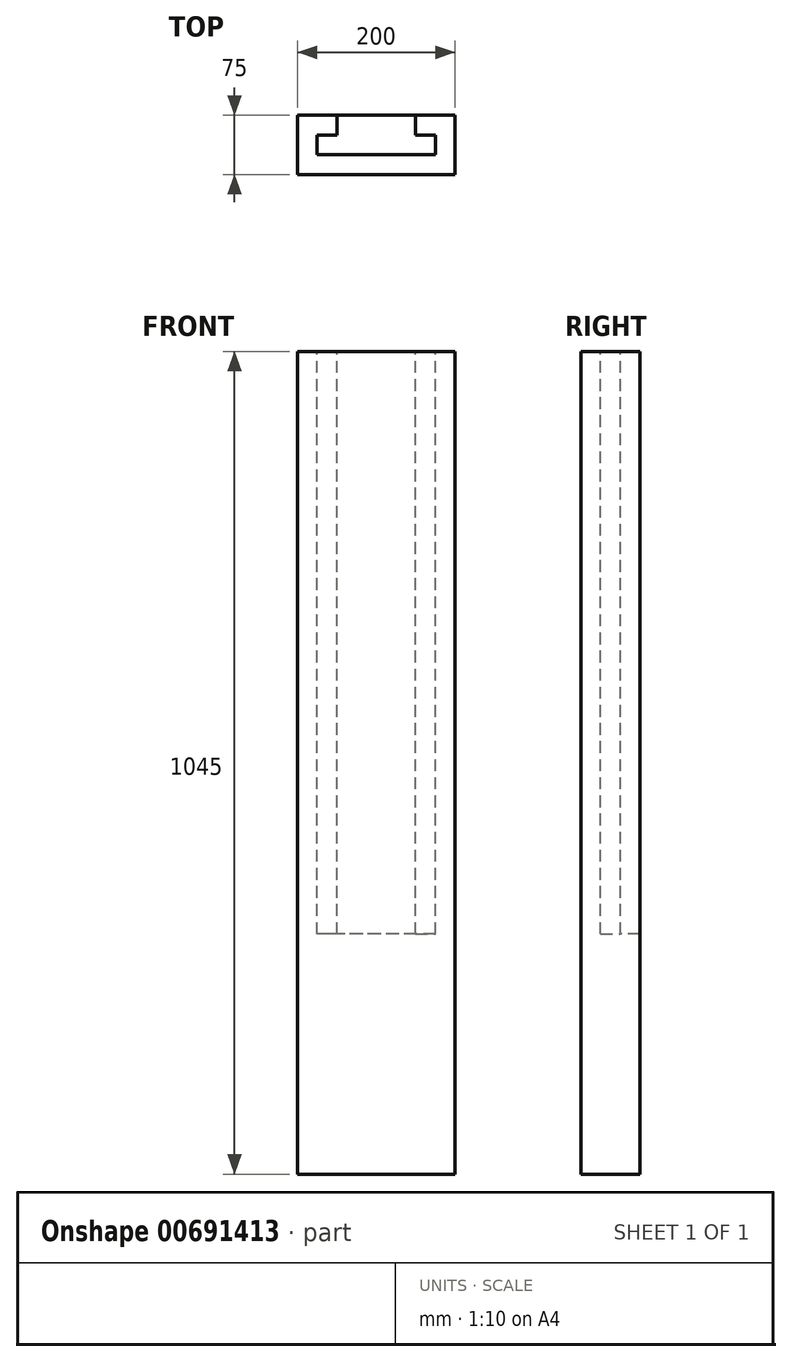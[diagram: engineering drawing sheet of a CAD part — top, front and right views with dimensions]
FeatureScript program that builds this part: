
annotation { "Feature Type Name" : "Feature", "Feature Type Description" : "" }
export const myFeature = defineFeature(function(context is Context, id is Id, definition is map)
    precondition{}
    {
        {
            var Q0;
            Q0=qCreatedBy(makeId("Right.planeOp"),FACE);
            var sketch = newSketch(context, id + "F0", { "sketchPlane" : qUnion([Q0])});
            skLineSegment(sketch, "E0.bottom", {"start": v(37.5, 305) * mm, "end": v(-37.5, 305) * mm});
            skLineSegment(sketch, "E0.top", {"start": v(37.5, -305) * mm, "end": v(-37.5, -305) * mm});
            skLineSegment(sketch, "E0.left", {"start": v(37.5, 305) * mm, "end": v(37.5, -305) * mm});
            skLineSegment(sketch, "E0.right", {"start": v(-37.5, 305) * mm, "end": v(-37.5, -305) * mm});
            skPoint(sketch, "E0.middle", {"position": v(0, 0) * mm});
            skSolve(sketch);
        }
        {
            var Q0;
            Q0=makeQuery(id+"F0.imprint","IMPRINT",FACE,{"disambiguationData":[TD([[makeQuery(id+"F0.imprint","IMPRINT",EDGE,{"derivedFrom":sQuery(id+"F0.wireOp",EDGE,"E0.bottom")}),1.0]])]});
            extrude(context, id + "F1", {"entities" : qUnion([Q0]), "depth" : 200 * mm, "offsetDistance" : 25 * mm});
        }
        {
            var Q0;
            Q0=makeQuery(id+"F1.opExtrude","SWEPT_FACE",FACE,{"disambiguationData":[OSD([sQuery(id+"F0.wireOp",EDGE,"E0.bottom")])]});
            var sketch = newSketch(context, id + "F2", { "sketchPlane" : qUnion([Q0])});
            skLineSegment(sketch, "E1.bottom", {"start": v(50, 37.5) * mm, "end": v(150, 37.5) * mm});
            skLineSegment(sketch, "E1.top", {"start": v(50, -12.5) * mm, "end": v(150, -12.5) * mm});
            skLineSegment(sketch, "E1.left", {"start": v(50, 37.5) * mm, "end": v(50, -12.5) * mm});
            skLineSegment(sketch, "E1.right", {"start": v(150, 37.5) * mm, "end": v(150, -12.5) * mm});
            skLineSegment(sketch, "E2.bottom", {"start": v(50, -12.5) * mm, "end": v(25, -12.5) * mm});
            skLineSegment(sketch, "E2.top", {"start": v(50, 12.5) * mm, "end": v(25, 12.5) * mm});
            skLineSegment(sketch, "E2.left", {"start": v(50, -12.5) * mm, "end": v(50, 12.5) * mm});
            skLineSegment(sketch, "E2.right", {"start": v(25, -12.5) * mm, "end": v(25, 12.5) * mm});
            skLineSegment(sketch, "E3.bottom", {"start": v(150, -12.5) * mm, "end": v(175, -12.5) * mm});
            skLineSegment(sketch, "E3.top", {"start": v(150, 12.5) * mm, "end": v(175, 12.5) * mm});
            skLineSegment(sketch, "E3.left", {"start": v(150, -12.5) * mm, "end": v(150, 12.5) * mm});
            skLineSegment(sketch, "E3.right", {"start": v(175, -12.5) * mm, "end": v(175, 12.5) * mm});
            skSolve(sketch);
        }
        {
            var Q0;
            Q0 = qSketchRegion(id + "F2", true);
            extrude(context, id + "F3", {"entities" : qUnion([Q0]), "operationType" : NewBodyOperationType.REMOVE, "oppositeDirection" : true, "depth" : 525 * mm, "offsetDistance" : 25 * mm});
        }
        {
            var Q0;
            Q0=makeQuery(id+"F1.opExtrude","SWEPT_FACE",FACE,{"disambiguationData":[OSD([sQuery(id+"F0.wireOp",EDGE,"E0.top")])]});
            var sketch = newSketch(context, id + "F4", { "sketchPlane" : qUnion([Q0])});
            skLineSegment(sketch, "E4.bottom", {"start": v(0, 37.5) * mm, "end": v(200, 37.5) * mm});
            skLineSegment(sketch, "E4.top", {"start": v(0, -37.5) * mm, "end": v(200, -37.5) * mm});
            skLineSegment(sketch, "E4.left", {"start": v(0, 37.5) * mm, "end": v(0, -37.5) * mm});
            skLineSegment(sketch, "E4.right", {"start": v(200, 37.5) * mm, "end": v(200, -37.5) * mm});
            skSolve(sketch);
        }
        {
            var Q0;
            Q0=makeQuery(id+"F4.imprint","IMPRINT",FACE,{"disambiguationData":[TD([[makeQuery(id+"F4.imprint","IMPRINT",EDGE,{"derivedFrom":sQuery(id+"F4.wireOp",EDGE,"E4.bottom")}),1.0]])]});
            extrude(context, id + "F5", {"entities" : qUnion([Q0]), "operationType" : NewBodyOperationType.ADD, "depth" : 220 * mm, "offsetDistance" : 25 * mm});
        }
        {
            var Q0;
            Q0=makeQuery(id+"F1.opExtrude","SWEPT_FACE",FACE,{"disambiguationData":[OSD([sQuery(id+"F0.wireOp",EDGE,"E0.bottom")])]});
            var sketch = newSketch(context, id + "F6", { "sketchPlane" : qUnion([Q0])});
            skLineSegment(sketch, "E5", {"start": v(25, 12.5) * mm, "end": v(50, 12.5) * mm});
            skLineSegment(sketch, "E6", {"start": v(50, 12.5) * mm, "end": v(50, 37.5) * mm});
            skLineSegment(sketch, "E7", {"start": v(50, 37.5) * mm, "end": v(0, 37.5) * mm});
            skLineSegment(sketch, "E8", {"start": v(0, 37.5) * mm, "end": v(0, -37.5) * mm});
            skLineSegment(sketch, "E9", {"start": v(0, -37.5) * mm, "end": v(200, -37.5) * mm});
            skLineSegment(sketch, "E10", {"start": v(200, -37.5) * mm, "end": v(200, 37.5) * mm});
            skLineSegment(sketch, "E11", {"start": v(200, 37.5) * mm, "end": v(150, 37.5) * mm});
            skLineSegment(sketch, "E12", {"start": v(150, 37.5) * mm, "end": v(150, 12.5) * mm});
            skLineSegment(sketch, "E13", {"start": v(150, 12.5) * mm, "end": v(175, 12.5) * mm});
            skLineSegment(sketch, "E14", {"start": v(175, 12.5) * mm, "end": v(175, -12.5) * mm});
            skLineSegment(sketch, "E15", {"start": v(175, -12.5) * mm, "end": v(25, -12.5) * mm});
            skLineSegment(sketch, "E16", {"start": v(25, -12.5) * mm, "end": v(25, 12.5) * mm});
            skSolve(sketch);
        }
        {
            var Q0;
            Q0=makeQuery(id+"F6.imprint","IMPRINT",FACE,{"disambiguationData":[TD([[makeQuery(id+"F6.imprint","IMPRINT",EDGE,{"derivedFrom":sQuery(id+"F6.wireOp",EDGE,"E5")}),-1.0]])]});
            extrude(context, id + "F7", {"entities" : qUnion([Q0]), "operationType" : NewBodyOperationType.ADD, "depth" : 215 * mm, "offsetDistance" : 25 * mm});
        }
    });
